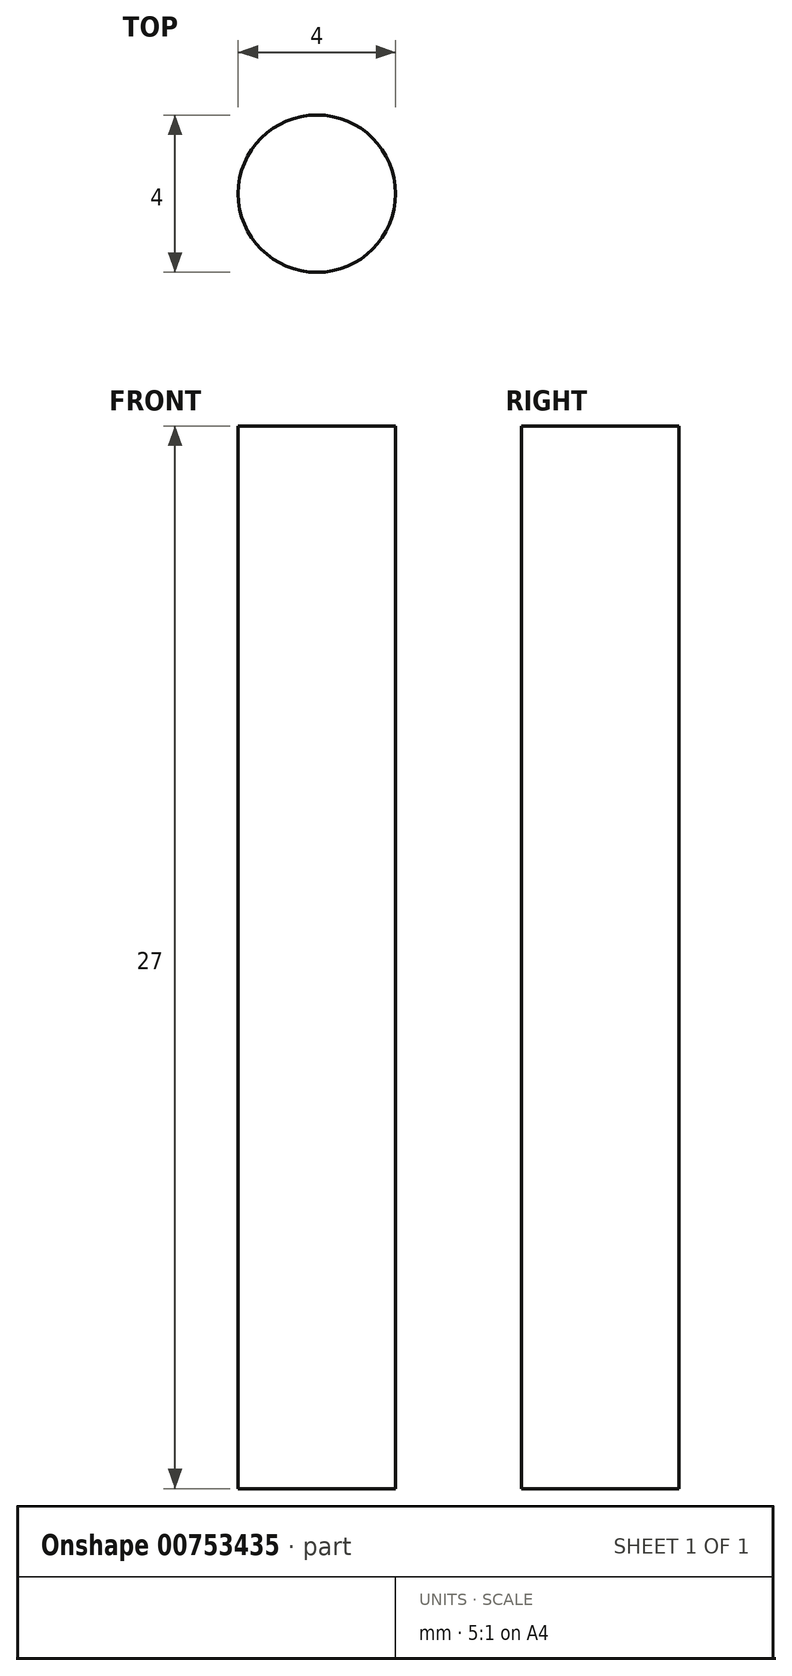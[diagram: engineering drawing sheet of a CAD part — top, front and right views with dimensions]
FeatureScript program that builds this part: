
annotation { "Feature Type Name" : "Feature", "Feature Type Description" : "" }
export const myFeature = defineFeature(function(context is Context, id is Id, definition is map)
    precondition{}
    {
        {
            var Q0;
            Q0=qCreatedBy(makeId("Top.planeOp"),FACE);
            var sketch = newSketch(context, id + "F0", { "sketchPlane" : qUnion([Q0])});
            skCircle(sketch, "E0", {"center": v(0, 0) * mm, "radius": 2 * mm});
            skSolve(sketch);
        }
        {
            var Q0;
            Q0=makeQuery(id+"F0.imprint","IMPRINT",FACE,{"disambiguationData":[TD([[makeQuery(id+"F0.imprint","IMPRINT",EDGE,{"derivedFrom":sQuery(id+"F0.wireOp",EDGE,"E0")}),1.0]])]});
            extrude(context, id + "F1", {"entities" : qUnion([Q0]), "depth" : 27 * mm, "offsetDistance" : 25 * mm});
        }
    });
